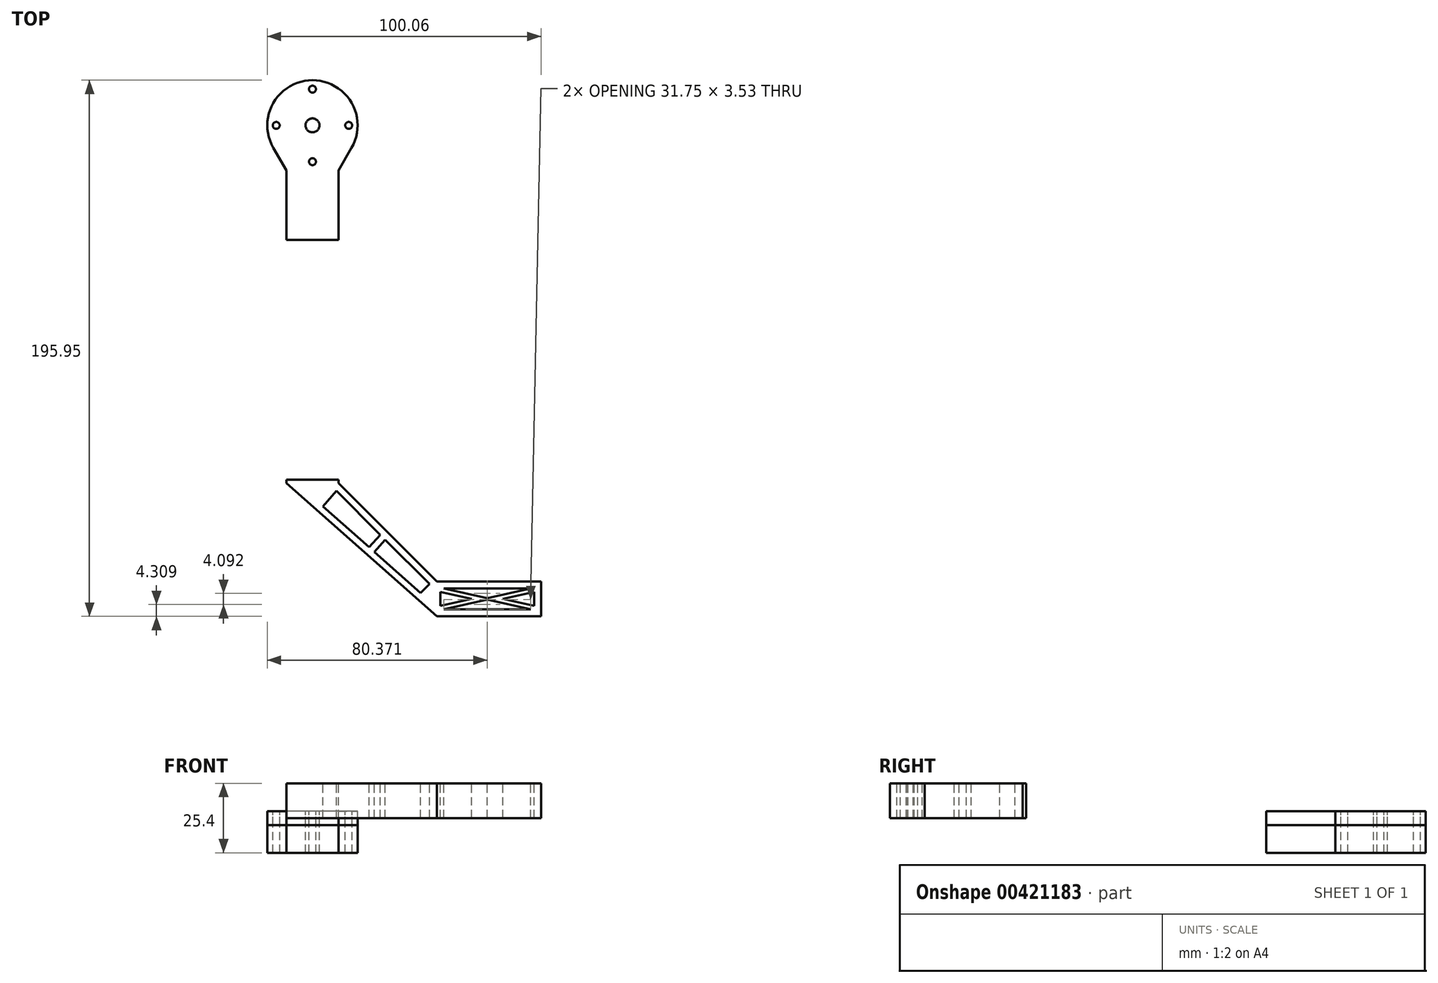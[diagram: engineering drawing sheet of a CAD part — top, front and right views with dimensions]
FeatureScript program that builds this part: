
annotation { "Feature Type Name" : "Feature", "Feature Type Description" : "" }
export const myFeature = defineFeature(function(context is Context, id is Id, definition is map)
    precondition{}
    {
        {
            var Q0;
            Q0=qCreatedBy(makeId("Top.planeOp"),FACE);
            var sketch = newSketch(context, id + "F0", { "sketchPlane" : qUnion([Q0])});
            skLineSegment(sketch, "E0", {"start": v(9.52, -92.96) * mm, "end": v(45.45, -128.89) * mm});
            skLineSegment(sketch, "E1", {"start": v(45.45, -128.89) * mm, "end": v(83.55, -128.89) * mm});
            skLineSegment(sketch, "E2", {"start": v(83.55, -128.89) * mm, "end": v(83.55, -141.59) * mm});
            skLineSegment(sketch, "E3", {"start": v(83.55, -141.59) * mm, "end": v(45.45, -141.59) * mm});
            skLineSegment(sketch, "E4", {"start": v(-9.53, -92.96) * mm, "end": v(45.45, -141.59) * mm});
            skLineSegment(sketch, "E5", {"start": v(-9.52, 21.34) * mm, "end": v(-14.3, 29.58) * mm});
            skLineSegment(sketch, "E6", {"start": v(9.52, 21.34) * mm, "end": v(14.3, 29.58) * mm});
            skArc(sketch, "E7", {"start": v(14.3, 29.58) * mm, "mid": v(0, 54.36) * mm, "end": v(-14.3, 29.58) * mm});
            skCircle(sketch, "E8", {"center": v(0, 51.1) * mm, "radius": 1.27 * mm});
            skCircle(sketch, "E9", {"center": v(0, 37.85) * mm, "radius": 2.54 * mm});
            skCircle(sketch, "E10.1.0", {"center": v(-13.25, 37.85) * mm, "radius": 1.27 * mm});
            skCircle(sketch, "E10.2.0", {"center": v(0, 24.6) * mm, "radius": 1.27 * mm});
            skCircle(sketch, "E10.3.0", {"center": v(13.25, 37.85) * mm, "radius": 1.27 * mm});
            skLineSegment(sketch, "E11", {"start": v(83.55, -141.59) * mm, "end": v(81, -141.59) * mm});
            skLineSegment(sketch, "E12", {"start": v(83.55, -128.89) * mm, "end": v(83.55, -131.43) * mm});
            skLineSegment(sketch, "E13", {"start": v(83.55, -131.43) * mm, "end": v(83.55, -139.05) * mm});
            skLineSegment(sketch, "E14", {"start": v(45.45, -141.59) * mm, "end": v(46.72, -141.59) * mm});
            skLineSegment(sketch, "E15", {"start": v(45.45, -128.89) * mm, "end": v(44.55, -127.99) * mm});
            skLineSegment(sketch, "E16", {"start": v(1.16, -102.42) * mm, "end": v(2.11, -103.26) * mm});
            skLineSegment(sketch, "E17", {"start": v(42.76, -129.78) * mm, "end": v(39.55, -132.98) * mm});
            skLineSegment(sketch, "E18", {"start": v(8.74, -95.77) * mm, "end": v(3.8, -101.36) * mm});
            skLineSegment(sketch, "E19.left", {"start": v(9.52, -92.96) * mm, "end": v(9.52, -91.7) * mm});
            skLineSegment(sketch, "E19.right", {"start": v(-9.53, -92.96) * mm, "end": v(-9.53, -91.7) * mm});
            skLineSegment(sketch, "E20", {"start": v(22.63, -118.01) * mm, "end": v(26.55, -113.57) * mm});
            skLineSegment(sketch, "E21", {"start": v(24.75, -111.78) * mm, "end": v(20.73, -116.33) * mm});
            skLineSegment(sketch, "E22", {"start": v(8.74, -95.77) * mm, "end": v(24.75, -111.78) * mm});
            skLineSegment(sketch, "E23", {"start": v(3.8, -101.36) * mm, "end": v(20.73, -116.33) * mm});
            skLineSegment(sketch, "E24", {"start": v(22.63, -118.01) * mm, "end": v(39.55, -132.98) * mm});
            skLineSegment(sketch, "E25", {"start": v(26.55, -113.57) * mm, "end": v(42.76, -129.78) * mm});
            skLineSegment(sketch, "E26", {"start": v(79.74, -131.43) * mm, "end": v(63.86, -134.95) * mm});
            skLineSegment(sketch, "E27", {"start": v(63.86, -134.95) * mm, "end": v(47.99, -131.43) * mm});
            skLineSegment(sketch, "E28", {"start": v(58.15, -135.24) * mm, "end": v(46.72, -132.7) * mm});
            skLineSegment(sketch, "E29", {"start": v(47.99, -139.05) * mm, "end": v(63.86, -135.52) * mm});
            skLineSegment(sketch, "E30", {"start": v(63.86, -135.52) * mm, "end": v(79.74, -139.05) * mm});
            skLineSegment(sketch, "E31", {"start": v(81, -137.78) * mm, "end": v(69.58, -135.24) * mm});
            skLineSegment(sketch, "E32", {"start": v(69.58, -135.24) * mm, "end": v(81, -132.7) * mm});
            skLineSegment(sketch, "E33", {"start": v(58.15, -135.24) * mm, "end": v(46.72, -137.78) * mm});
            skLineSegment(sketch, "E34", {"start": v(46.72, -132.7) * mm, "end": v(46.72, -137.78) * mm});
            skLineSegment(sketch, "E35", {"start": v(47.99, -139.05) * mm, "end": v(79.74, -139.05) * mm});
            skLineSegment(sketch, "E36", {"start": v(81, -132.7) * mm, "end": v(81, -137.78) * mm});
            skLineSegment(sketch, "E37", {"start": v(79.74, -131.43) * mm, "end": v(47.99, -131.43) * mm});
            skLineSegment(sketch, "E38", {"start": v(9.52, -91.7) * mm, "end": v(9.52, 21.34) * mm});
            skLineSegment(sketch, "E39", {"start": v(-9.53, -91.7) * mm, "end": v(-9.52, 21.34) * mm});
            skLineSegment(sketch, "E40", {"start": v(-9.52, 21.34) * mm, "end": v(-9.53, 2.73) * mm});
            skLineSegment(sketch, "E41", {"start": v(9.52, 21.34) * mm, "end": v(9.52, -4.05) * mm});
            skLineSegment(sketch, "E42", {"start": v(9.52, -4.05) * mm, "end": v(-9.53, -4.05) * mm});
            skLineSegment(sketch, "E43.bottom", {"start": v(-9.53, -4.05) * mm, "end": v(-9.53, -4.05) * mm});
            skLineSegment(sketch, "E43.top", {"start": v(-9.53, -6.59) * mm, "end": v(-9.53, -6.59) * mm});
            skLineSegment(sketch, "E43.left", {"start": v(-9.53, -4.05) * mm, "end": v(-9.53, -6.59) * mm});
            skLineSegment(sketch, "E43.right", {"start": v(-9.53, -4.05) * mm, "end": v(-9.53, -6.59) * mm});
            skLineSegment(sketch, "E44", {"start": v(-9.53, -6.59) * mm, "end": v(-9.53, -7.86) * mm});
            skLineSegment(sketch, "E45", {"start": v(-5.7, -90.42) * mm, "end": v(0, -56.15) * mm});
            skLineSegment(sketch, "E46", {"start": v(0, -56.15) * mm, "end": v(5.72, -90.42) * mm});
            skLineSegment(sketch, "E47", {"start": v(6.99, -9.13) * mm, "end": v(0.21, -49.77) * mm});
            skLineSegment(sketch, "E48", {"start": v(5.72, -7.86) * mm, "end": v(0, -42.13) * mm});
            skLineSegment(sketch, "E49", {"start": v(0, -42.13) * mm, "end": v(-5.7, -7.86) * mm});
            skLineSegment(sketch, "E50", {"start": v(-0.21, -49.77) * mm, "end": v(-6.99, -9.13) * mm});
            skLineSegment(sketch, "E51", {"start": v(6.77, -89.14) * mm, "end": v(0.21, -49.77) * mm});
            skLineSegment(sketch, "E52", {"start": v(-0.21, -49.77) * mm, "end": v(-6.77, -89.14) * mm});
            skLineSegment(sketch, "E53", {"start": v(-5.7, -7.86) * mm, "end": v(5.72, -7.86) * mm});
            skLineSegment(sketch, "E54", {"start": v(6.99, -9.13) * mm, "end": v(6.77, -89.14) * mm});
            skLineSegment(sketch, "E55", {"start": v(5.72, -90.42) * mm, "end": v(-5.7, -90.42) * mm});
            skLineSegment(sketch, "E56", {"start": v(-6.77, -89.14) * mm, "end": v(-6.99, -9.13) * mm});
            skLineSegment(sketch, "E57", {"start": v(-9.53, -91.7) * mm, "end": v(9.52, -91.7) * mm});
            skSolve(sketch);
        }
        {
            var Q0;
            Q0=makeQuery(id+"F0.imprint","IMPRINT",FACE,{"disambiguationData":[TD([[makeQuery(id+"F0.imprint","IMPRINT",EDGE,{"derivedFrom":sQuery(id+"F0.wireOp",EDGE,"E38")}),1.0]])]});
            extrude(context, id + "F1", {"entities" : qUnion([Q0]), "oppositeDirection" : true, "depth" : 25.4 * mm});
        }
        {
            var Q0;
            Q0=makeQuery(id+"F0.imprint","IMPRINT",FACE,{"disambiguationData":[TD([[makeQuery(id+"F0.imprint","IMPRINT",EDGE,{"derivedFrom":sQuery(id+"F0.wireOp",EDGE,"E5")}),-1.0]])]});
            extrude(context, id + "F2", {"entities" : qUnion([Q0]), "oppositeDirection" : true, "depth" : 15.24 * mm});
        }
        {
            var Q0;
            Q0=makeQuery(id+"F0.imprint","IMPRINT",FACE,{"disambiguationData":[TD([[makeQuery(id+"F0.imprint","IMPRINT",EDGE,{"derivedFrom":sQuery(id+"F0.wireOp",EDGE,"E5")}),-1.0]])]});
            extrude(context, id + "F3", {"entities" : qUnion([Q0]), "operationType" : NewBodyOperationType.REMOVE, "oppositeDirection" : true, "depth" : 10.16 * mm});
        }
        {
            var Q0;
            Q0=makeQuery(id+"F0.imprint","IMPRINT",FACE,{"disambiguationData":[TD([[makeQuery(id+"F0.imprint","IMPRINT",EDGE,{"derivedFrom":sQuery(id+"F0.wireOp",EDGE,"E0")}),-1.0]])]});
            extrude(context, id + "F4", {"entities" : qUnion([Q0]), "oppositeDirection" : true, "depth" : 12.7 * mm});
        }
    });
